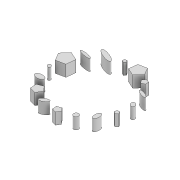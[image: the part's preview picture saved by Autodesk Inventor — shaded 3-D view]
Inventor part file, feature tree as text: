
AUTODESK INVENTOR PART (.ipt)
format: ipt  version: 2021 (Build 250183000, 183)  size: 166,912 bytes
history: native  units: in
note: dims shown in document units (in); Inventor stores cm internally (conversion verified against a paired STEP export)
features: extrude x1, sketch x1
ambient origin geometry x8: Origin, YZ Plane, XZ Plane, XY Plane, X Axis, Y Axis, Z Axis, Center Point
bodies: Solid1 (feature_tree)
feature tree (2):
  extrude  "Extrusion1"  Depth=118.1102in TaperAngle=360.0deg
  sketch  "Sketch1"  dims[d0=787.4016in d1=6.2992in d3=360.0deg d5=118.1102in d6=0.0in]
